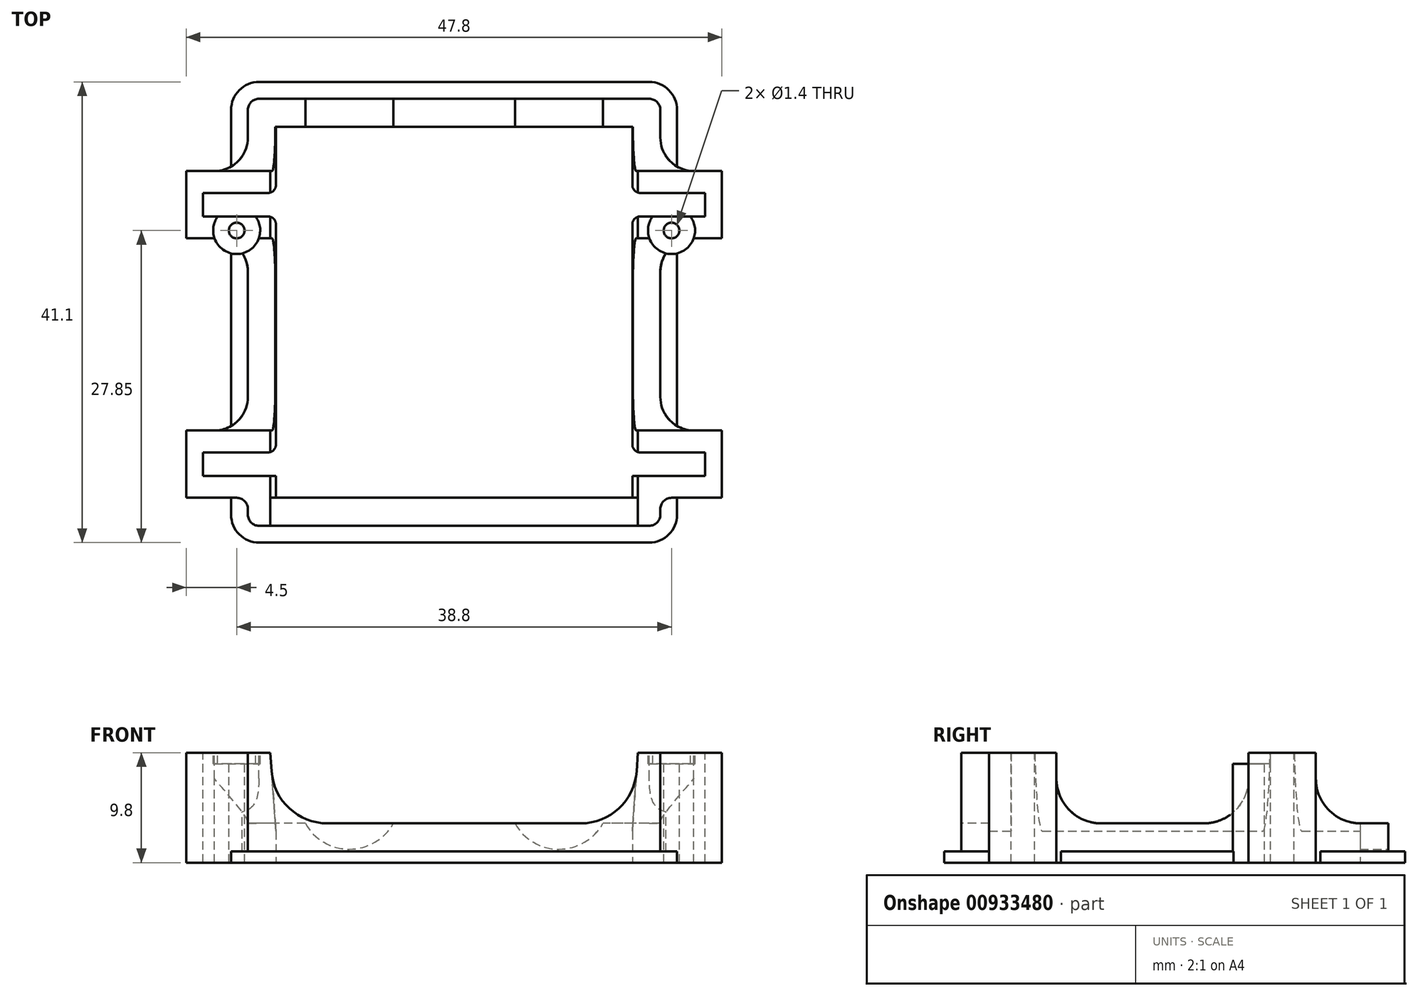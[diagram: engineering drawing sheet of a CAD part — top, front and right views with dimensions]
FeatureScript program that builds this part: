
annotation { "Feature Type Name" : "Feature", "Feature Type Description" : "" }
export const myFeature = defineFeature(function(context is Context, id is Id, definition is map)
    precondition{}
    {
        {
            assignVariable(context, id + "F0", {"name" : "ServoT", "anyValue" : 9.8});
        }
        {
            assignVariable(context, id + "F1", {"name" : "GlueEdgeH", "anyValue" : 1});
        }
        {
            var Q0;
            Q0=qCreatedBy(makeId("Top.planeOp"),FACE);
            var sketch = newSketch(context, id + "F2", { "sketchPlane" : qUnion([Q0])});
            skLineSegment(sketch, "E0.bottom", {"start": v(15.9, -16.55) * mm, "end": v(-15.9, -16.55) * mm});
            skLineSegment(sketch, "E0.top", {"start": v(15.9, 16.55) * mm, "end": v(-15.9, 16.55) * mm});
            skLineSegment(sketch, "E0.left", {"start": v(15.9, -16.55) * mm, "end": v(15.9, 16.55) * mm});
            skLineSegment(sketch, "E0.right", {"start": v(-15.9, -16.55) * mm, "end": v(-15.9, 16.55) * mm});
            skPoint(sketch, "E0.middle", {"position": v(0, 0) * mm});
            skLineSegment(sketch, "E1.0", {"start": v(17.4, 19.05) * mm, "end": v(-17.4, 19.05) * mm});
            skLineSegment(sketch, "E1.1", {"start": v(18.4, -18.05) * mm, "end": v(18.4, -17.55) * mm});
            skLineSegment(sketch, "E1.2", {"start": v(17.4, -19.05) * mm, "end": v(-17.4, -19.05) * mm});
            skLineSegment(sketch, "E1.3", {"start": v(-18.4, -18.05) * mm, "end": v(-18.4, -17.55) * mm});
            skLineSegment(sketch, "E2", {"start": v(-26.72, 9.6) * mm, "end": v(24.49, 9.6) * mm, "construction": true});
            skLineSegment(sketch, "E3", {"start": v(-23.9, 6.6) * mm, "end": v(-23.9, 12.6) * mm});
            skLineSegment(sketch, "E4", {"start": v(23.9, 6.6) * mm, "end": v(23.9, 12.6) * mm});
            skPoint(sketch, "E5", {"position": v(-23.9, 9.6) * mm});
            skPoint(sketch, "E6", {"position": v(23.9, 9.6) * mm});
            skLineSegment(sketch, "E7", {"start": v(-23.9, 12.6) * mm, "end": v(-21.4, 12.6) * mm});
            skLineSegment(sketch, "E8", {"start": v(-23.9, 6.6) * mm, "end": v(-21.4, 6.6) * mm});
            skLineSegment(sketch, "E9", {"start": v(23.9, 12.6) * mm, "end": v(21.4, 12.6) * mm});
            skLineSegment(sketch, "E10", {"start": v(23.9, 6.6) * mm, "end": v(21.4, 6.6) * mm});
            skLineSegment(sketch, "E11.trimOffspring", {"start": v(-18.4, 15.6) * mm, "end": v(-18.4, 18.05) * mm});
            skLineSegment(sketch, "E12.trimOffspring", {"start": v(18.4, 15.6) * mm, "end": v(18.4, 18.05) * mm});
            skPoint(sketch, "E13.visualSharp", {"position": v(-18.4, 6.6) * mm});
            skArc(sketch, "E13.filletArc", {"start": v(-18.4, 3.6) * mm, "mid": v(-19.28, 5.72) * mm, "end": v(-21.4, 6.6) * mm});
            skPoint(sketch, "E14.visualSharp", {"position": v(-18.4, 12.6) * mm});
            skArc(sketch, "E14.filletArc", {"start": v(-21.4, 12.6) * mm, "mid": v(-19.28, 13.48) * mm, "end": v(-18.4, 15.6) * mm});
            skPoint(sketch, "E15.visualSharp", {"position": v(18.4, 12.6) * mm});
            skArc(sketch, "E15.filletArc", {"start": v(18.4, 15.6) * mm, "mid": v(19.28, 13.48) * mm, "end": v(21.4, 12.6) * mm});
            skPoint(sketch, "E16.visualSharp", {"position": v(18.4, 6.6) * mm});
            skArc(sketch, "E16.filletArc", {"start": v(21.4, 6.6) * mm, "mid": v(19.28, 5.72) * mm, "end": v(18.4, 3.6) * mm});
            skPoint(sketch, "E17.visualSharp", {"position": v(-18.4, 19.05) * mm});
            skArc(sketch, "E17.filletArc", {"start": v(-17.4, 19.05) * mm, "mid": v(-18.1, 18.76) * mm, "end": v(-18.4, 18.05) * mm});
            skPoint(sketch, "E18.visualSharp", {"position": v(18.4, 19.05) * mm});
            skArc(sketch, "E18.filletArc", {"start": v(18.4, 18.05) * mm, "mid": v(18.1, 18.76) * mm, "end": v(17.4, 19.05) * mm});
            skPoint(sketch, "E19.visualSharp", {"position": v(18.4, -19.05) * mm});
            skArc(sketch, "E19.filletArc", {"start": v(17.4, -19.05) * mm, "mid": v(18.1, -18.76) * mm, "end": v(18.4, -18.05) * mm});
            skPoint(sketch, "E20.visualSharp", {"position": v(-18.4, -19.05) * mm});
            skArc(sketch, "E20.filletArc", {"start": v(-18.4, -18.05) * mm, "mid": v(-18.1, -18.76) * mm, "end": v(-17.4, -19.05) * mm});
            skLineSegment(sketch, "E21", {"start": v(0, -21.27) * mm, "end": v(0, 18.53) * mm, "construction": true});
            skPoint(sketch, "E21.endSnap0", {"position": v(0, -19.05) * mm});
            skLineSegment(sketch, "E22", {"start": v(-21.4, 0.48) * mm, "end": v(-21.4, 19.4) * mm, "construction": true});
            skLineSegment(sketch, "E23", {"start": v(21.4, 14.16) * mm, "end": v(21.4, -1.16) * mm, "construction": true});
            skLineSegment(sketch, "E24", {"start": v(-26.28, -13.55) * mm, "end": v(27.26, -13.55) * mm, "construction": true});
            skLineSegment(sketch, "E25", {"start": v(-23.9, -10.55) * mm, "end": v(-23.9, -16.55) * mm});
            skLineSegment(sketch, "E26", {"start": v(23.9, -10.55) * mm, "end": v(23.9, -16.55) * mm});
            skPoint(sketch, "E27", {"position": v(-23.9, -13.55) * mm});
            skPoint(sketch, "E28", {"position": v(23.9, -13.55) * mm});
            skLineSegment(sketch, "E29", {"start": v(-23.9, -10.55) * mm, "end": v(-21.4, -10.55) * mm});
            skLineSegment(sketch, "E30", {"start": v(-23.9, -16.55) * mm, "end": v(-19.4, -16.55) * mm});
            skLineSegment(sketch, "E31", {"start": v(23.9, -10.55) * mm, "end": v(21.4, -10.55) * mm});
            skLineSegment(sketch, "E32", {"start": v(23.9, -16.55) * mm, "end": v(19.4, -16.55) * mm});
            skLineSegment(sketch, "E33.trimOffspring", {"start": v(-18.4, -7.55) * mm, "end": v(-18.4, 3.6) * mm});
            skLineSegment(sketch, "E34.trimOffspring", {"start": v(18.4, -7.55) * mm, "end": v(18.4, 3.6) * mm});
            skPoint(sketch, "E35.visualSharp", {"position": v(-18.4, -10.55) * mm});
            skArc(sketch, "E35.filletArc", {"start": v(-21.4, -10.55) * mm, "mid": v(-19.28, -9.67) * mm, "end": v(-18.4, -7.55) * mm});
            skPoint(sketch, "E36.visualSharp", {"position": v(18.4, -10.55) * mm});
            skArc(sketch, "E36.filletArc", {"start": v(18.4, -7.55) * mm, "mid": v(19.28, -9.67) * mm, "end": v(21.4, -10.55) * mm});
            skPoint(sketch, "E37.visualSharp", {"position": v(-18.4, -16.55) * mm});
            skArc(sketch, "E37.filletArc", {"start": v(-18.4, -17.55) * mm, "mid": v(-18.7, -16.84) * mm, "end": v(-19.4, -16.55) * mm});
            skPoint(sketch, "E38.visualSharp", {"position": v(18.4, -16.55) * mm});
            skArc(sketch, "E38.filletArc", {"start": v(19.4, -16.55) * mm, "mid": v(18.7, -16.84) * mm, "end": v(18.4, -17.55) * mm});
            skSolve(sketch);
        }
        {
            var Q0;
            Q0=qSketchRegion(id+"F2",true);
            extrude(context, id + "F3", {"entities" : qUnion([Q0]), "depth" : (getVariable(context, 'ServoT')) * mm, "offsetDistance" : 25 * mm});
        }
        {
            var Q0;
            Q0=makeQuery(id+"F3.opExtrude","SWEPT_FACE",FACE,{"disambiguationData":[OSD([sQuery(id+"F2.wireOp",EDGE,"E1.3")])]});
            var sketch = newSketch(context, id + "F4", { "sketchPlane" : qUnion([Q0])});
            skLineSegment(sketch, "E39.0", {"start": v(-19.05, 9.8) * mm, "end": v(-19.05, 3.5) * mm});
            skLineSegment(sketch, "E40.0", {"start": v(-19.05, 9.8) * mm, "end": v(-18.05, 9.8) * mm});
            skLineSegment(sketch, "E41.0", {"start": v(-15.6, 9.8) * mm, "end": v(-18.05, 9.8) * mm});
            skLineSegment(sketch, "E42.0", {"start": v(-12.6, 9.8) * mm, "end": v(-15.6, 9.8) * mm});
            skLineSegment(sketch, "E43.0", {"start": v(-12.6, 9.8) * mm, "end": v(-12.6, 7.5) * mm});
            skLineSegment(sketch, "E44", {"start": v(-19.05, 3.5) * mm, "end": v(-16.6, 3.5) * mm});
            skPoint(sketch, "E45.visualSharp", {"position": v(-12.6, 3.5) * mm});
            skArc(sketch, "E45.filletArc", {"start": v(-16.6, 3.5) * mm, "mid": v(-13.77, 4.67) * mm, "end": v(-12.6, 7.5) * mm});
            skLineSegment(sketch, "E46", {"start": v(-2.6, 3.5) * mm, "end": v(6.55, 3.5) * mm});
            skLineSegment(sketch, "E47.0", {"start": v(-6.6, 9.8) * mm, "end": v(-6.6, 7.5) * mm});
            skLineSegment(sketch, "E48.0", {"start": v(10.55, 9.8) * mm, "end": v(10.55, 7.5) * mm});
            skLineSegment(sketch, "E49.0", {"start": v(7.55, 9.8) * mm, "end": v(-6.6, 9.8) * mm});
            skLineSegment(sketch, "E50.0", {"start": v(10.55, 9.8) * mm, "end": v(7.55, 9.8) * mm});
            skPoint(sketch, "E51.orphan", {"position": v(10.55, 0) * mm});
            skPoint(sketch, "E52.visualSharp", {"position": v(10.55, 3.5) * mm});
            skArc(sketch, "E52.filletArc", {"start": v(6.55, 3.5) * mm, "mid": v(9.38, 4.67) * mm, "end": v(10.55, 7.5) * mm});
            skPoint(sketch, "E53.visualSharp", {"position": v(-6.6, 3.5) * mm});
            skArc(sketch, "E53.filletArc", {"start": v(-6.6, 7.5) * mm, "mid": v(-5.43, 4.67) * mm, "end": v(-2.6, 3.5) * mm});
            skSolve(sketch);
        }
        {
            var Q0;
            Q0=qSketchRegion(id+"F4",true);
            extrude(context, id + "F5", {"entities" : qUnion([Q0]), "operationType" : NewBodyOperationType.REMOVE, "endBound" : BoundingType.THROUGH_ALL, "oppositeDirection" : true, "depth" : 25 * mm, "offsetDistance" : 25 * mm, "hasSecondDirection" : true, "secondDirectionBound" : SecondDirectionBoundingType.THROUGH_ALL, "secondDirectionOppositeDirection" : false, "secondDirectionDepth" : 25 * mm});
        }
        {
            var Q0;
            Q0=makeQuery(id+"F3.opExtrude","CAP_FACE",FACE,{"disambiguationData":[OSD([sQuery(id+"F2.wireOp",EDGE,"E0.bottom"),sQuery(id+"F2.wireOp",EDGE,"E0.top"),sQuery(id+"F2.wireOp",EDGE,"E0.left"),sQuery(id+"F2.wireOp",EDGE,"E0.right"),sQuery(id+"F2.wireOp",EDGE,"E1.0"),sQuery(id+"F2.wireOp",EDGE,"E1.1"),sQuery(id+"F2.wireOp",EDGE,"E1.2"),sQuery(id+"F2.wireOp",EDGE,"E1.3"),sQuery(id+"F2.wireOp",EDGE,"E3"),sQuery(id+"F2.wireOp",EDGE,"E4"),sQuery(id+"F2.wireOp",EDGE,"E7"),sQuery(id+"F2.wireOp",EDGE,"E8"),sQuery(id+"F2.wireOp",EDGE,"E9"),sQuery(id+"F2.wireOp",EDGE,"E10"),sQuery(id+"F2.wireOp",EDGE,"E11.trimOffspring"),sQuery(id+"F2.wireOp",EDGE,"E12.trimOffspring"),sQuery(id+"F2.wireOp",EDGE,"E13.filletArc"),sQuery(id+"F2.wireOp",EDGE,"E14.filletArc"),sQuery(id+"F2.wireOp",EDGE,"E15.filletArc"),sQuery(id+"F2.wireOp",EDGE,"E16.filletArc"),sQuery(id+"F2.wireOp",EDGE,"E17.filletArc"),sQuery(id+"F2.wireOp",EDGE,"E18.filletArc"),sQuery(id+"F2.wireOp",EDGE,"E19.filletArc"),sQuery(id+"F2.wireOp",EDGE,"E20.filletArc")])],"isStart":true});
            var sketch = newSketch(context, id + "F6", { "sketchPlane" : qUnion([Q0])});
            skLineSegment(sketch, "E54.0", {"start": v(17.4, 19.05) * mm, "end": v(-17.4, 19.05) * mm});
            skArc(sketch, "E55.0", {"start": v(-18.4, 18.05) * mm, "mid": v(-18.1, 18.76) * mm, "end": v(-17.4, 19.05) * mm});
            skLineSegment(sketch, "E56.0", {"start": v(-18.4, 18.05) * mm, "end": v(-18.4, -6.6) * mm});
            skArc(sketch, "E57.0", {"start": v(17.4, 19.05) * mm, "mid": v(18.1, 18.76) * mm, "end": v(18.4, 18.05) * mm});
            skLineSegment(sketch, "E58.0", {"start": v(18.4, 18.05) * mm, "end": v(18.4, -6.6) * mm});
            skLineSegment(sketch, "E59.0", {"start": v(18.4, -12.6) * mm, "end": v(18.4, -18.05) * mm});
            skArc(sketch, "E60.0", {"start": v(18.4, -18.05) * mm, "mid": v(18.1, -18.76) * mm, "end": v(17.4, -19.05) * mm});
            skLineSegment(sketch, "E61.0", {"start": v(17.4, -19.05) * mm, "end": v(-17.4, -19.05) * mm});
            skArc(sketch, "E62.0", {"start": v(-17.4, -19.05) * mm, "mid": v(-18.1, -18.76) * mm, "end": v(-18.4, -18.05) * mm});
            skLineSegment(sketch, "E63.0", {"start": v(-18.4, -12.6) * mm, "end": v(-18.4, -18.05) * mm});
            skLineSegment(sketch, "E64.0", {"start": v(-19.9, 18.05) * mm, "end": v(-19.9, -6.6) * mm});
            skLineSegment(sketch, "E64.1", {"start": v(19.9, 18.05) * mm, "end": v(19.9, -6.6) * mm});
            skArc(sketch, "E64.2", {"start": v(17.4, 20.55) * mm, "mid": v(19.17, 19.82) * mm, "end": v(19.9, 18.05) * mm});
            skLineSegment(sketch, "E64.3", {"start": v(17.4, 20.55) * mm, "end": v(-17.4, 20.55) * mm});
            skArc(sketch, "E64.4", {"start": v(-19.9, 18.05) * mm, "mid": v(-19.17, 19.82) * mm, "end": v(-17.4, 20.55) * mm});
            skLineSegment(sketch, "E65.0", {"start": v(19.9, -12.6) * mm, "end": v(19.9, -18.05) * mm});
            skLineSegment(sketch, "E65.1", {"start": v(-19.9, -12.6) * mm, "end": v(-19.9, -18.05) * mm});
            skArc(sketch, "E65.2", {"start": v(-17.4, -20.55) * mm, "mid": v(-19.17, -19.82) * mm, "end": v(-19.9, -18.05) * mm});
            skLineSegment(sketch, "E65.3", {"start": v(17.4, -20.55) * mm, "end": v(-17.4, -20.55) * mm});
            skArc(sketch, "E65.4", {"start": v(19.9, -18.05) * mm, "mid": v(19.17, -19.82) * mm, "end": v(17.4, -20.55) * mm});
            skLineSegment(sketch, "E66", {"start": v(-18.4, -6.6) * mm, "end": v(-19.9, -6.6) * mm});
            skLineSegment(sketch, "E67", {"start": v(-18.4, -12.6) * mm, "end": v(-19.9, -12.6) * mm});
            skLineSegment(sketch, "E68", {"start": v(19.9, -12.6) * mm, "end": v(18.4, -12.6) * mm});
            skLineSegment(sketch, "E69", {"start": v(19.9, -6.6) * mm, "end": v(18.4, -6.6) * mm});
            skSolve(sketch);
        }
        {
            var Q0;
            Q0=qSketchRegion(id+"F6",true);
            extrude(context, id + "F7", {"entities" : qUnion([Q0]), "operationType" : NewBodyOperationType.ADD, "oppositeDirection" : true, "depth" : (getVariable(context, 'GlueEdgeH')) * mm, "offsetDistance" : 25 * mm});
        }
        {
            var Q0;
            {var subQ0=sQuery(id+"F2.wireOp",EDGE,"E0.right");var subQ1=sQuery(id+"F2.wireOp",EDGE,"E13.filletArc");var subQ2=sQuery(id+"F2.wireOp",EDGE,"E3");Q0=makeQuery(id+"F5.boolean.opBoolean","SPLIT",FACE,{"disambiguationData":[TD([makeQuery(id+"F3.opExtrude","SWEPT_FACE",FACE,{"disambiguationData":[OSD([subQ0])]})])],"derivedFrom":makeQuery(id+"F3.opExtrude","CAP_FACE",FACE,{"disambiguationData":[OSD([sQuery(id+"F2.wireOp",EDGE,"E0.bottom"),sQuery(id+"F2.wireOp",EDGE,"E0.top"),sQuery(id+"F2.wireOp",EDGE,"E0.left"),subQ0,sQuery(id+"F2.wireOp",EDGE,"E1.0"),sQuery(id+"F2.wireOp",EDGE,"E1.1"),sQuery(id+"F2.wireOp",EDGE,"E1.2"),sQuery(id+"F2.wireOp",EDGE,"E1.3"),subQ2,sQuery(id+"F2.wireOp",EDGE,"E4"),sQuery(id+"F2.wireOp",EDGE,"E11.trimOffspring"),sQuery(id+"F2.wireOp",EDGE,"E12.trimOffspring"),subQ1,sQuery(id+"F2.wireOp",EDGE,"E14.filletArc"),sQuery(id+"F2.wireOp",EDGE,"E15.filletArc"),sQuery(id+"F2.wireOp",EDGE,"E16.filletArc"),sQuery(id+"F2.wireOp",EDGE,"E17.filletArc"),sQuery(id+"F2.wireOp",EDGE,"E18.filletArc"),sQuery(id+"F2.wireOp",EDGE,"E19.filletArc"),sQuery(id+"F2.wireOp",EDGE,"E20.filletArc")])],"isStart":false})});}
            var sketch = newSketch(context, id + "F8", { "sketchPlane" : qUnion([Q0])});
            skLineSegment(sketch, "E70.0", {"start": v(-26.72, 9.6) * mm, "end": v(24.49, 9.6) * mm, "construction": true});
            skLineSegment(sketch, "E71.0", {"start": v(-15.9, 8.55) * mm, "end": v(-15.9, 10.65) * mm});
            skLineSegment(sketch, "E72.0", {"start": v(15.9, 8.55) * mm, "end": v(15.9, 10.65) * mm});
            skLineSegment(sketch, "E73", {"start": v(-22.4, 10.65) * mm, "end": v(-15.9, 10.65) * mm});
            skLineSegment(sketch, "E74", {"start": v(-22.4, 8.55) * mm, "end": v(-15.9, 8.55) * mm});
            skLineSegment(sketch, "E75", {"start": v(15.9, 10.65) * mm, "end": v(22.4, 10.65) * mm});
            skLineSegment(sketch, "E76", {"start": v(15.9, 8.55) * mm, "end": v(22.4, 8.55) * mm});
            skPoint(sketch, "E77.orphan", {"position": v(-23.9, 12.6) * mm});
            skPoint(sketch, "E78.orphan", {"position": v(-23.9, 6.6) * mm});
            skPoint(sketch, "E79.orphan", {"position": v(23.9, 12.6) * mm});
            skPoint(sketch, "E80.orphan", {"position": v(23.9, 6.6) * mm});
            skLineSegment(sketch, "E81", {"start": v(-22.4, 10.65) * mm, "end": v(-22.4, 8.55) * mm});
            skPoint(sketch, "E82", {"position": v(-15.9, 9.6) * mm});
            skPoint(sketch, "E83", {"position": v(15.9, 9.6) * mm});
            skLineSegment(sketch, "E84", {"start": v(22.4, 10.65) * mm, "end": v(22.4, 8.55) * mm});
            skLineSegment(sketch, "E85.0", {"start": v(-26.28, -13.55) * mm, "end": v(27.26, -13.55) * mm, "construction": true});
            skLineSegment(sketch, "E86", {"start": v(-22.4, -12.5) * mm, "end": v(-22.4, -14.6) * mm});
            skLineSegment(sketch, "E87", {"start": v(22.4, -12.5) * mm, "end": v(22.4, -14.6) * mm});
            skPoint(sketch, "E88", {"position": v(-22.4, -13.55) * mm});
            skPoint(sketch, "E89", {"position": v(22.4, -13.55) * mm});
            skLineSegment(sketch, "E90", {"start": v(-22.4, -12.5) * mm, "end": v(-15.9, -12.5) * mm});
            skLineSegment(sketch, "E91", {"start": v(22.4, -14.6) * mm, "end": v(15.9, -14.6) * mm});
            skLineSegment(sketch, "E92.0", {"start": v(-15.9, -14.6) * mm, "end": v(-15.9, -12.5) * mm});
            skLineSegment(sketch, "E93.0", {"start": v(15.9, -14.6) * mm, "end": v(15.9, -12.5) * mm});
            skLineSegment(sketch, "E94.trimOffspring", {"start": v(15.9, -12.5) * mm, "end": v(22.4, -12.5) * mm});
            skLineSegment(sketch, "E95.trimOffspring", {"start": v(-15.9, -14.6) * mm, "end": v(-22.4, -14.6) * mm});
            skSolve(sketch);
        }
        {
            var Q0;
            Q0=qSketchRegion(id+"F8",true);
            extrude(context, id + "F9", {"entities" : qUnion([Q0]), "operationType" : NewBodyOperationType.REMOVE, "oppositeDirection" : true, "depth" : (getVariable(context, 'ServoT')) * mm, "offsetDistance" : 25 * mm});
        }
        {
            var Q0;
            {var subQ1=sQuery(id+"F2.wireOp",EDGE,"E7");var subQ2=sQuery(id+"F2.wireOp",EDGE,"E0.right");var subQ4=makeQuery(id+"F3.opExtrude","SWEPT_FACE",FACE,{"disambiguationData":[OSD([subQ1])]});Q0=makeQuery(id+"F9.boolean.opBoolean","SPLIT",EDGE,{"disambiguationData":[TD([subQ4])],"derivedFrom":makeQuery(id+"F5.boolean.opBoolean","SPLIT",EDGE,{"disambiguationData":[TD([subQ4])],"derivedFrom":makeQuery(id+"F3.opExtrude","CAP_EDGE",EDGE,{"disambiguationData":[OSD([subQ2])],"isStart":false})})});}
            var Q1;
            {var subQ0=sQuery(id+"F2.wireOp",EDGE,"E8");var subQ1=sQuery(id+"F2.wireOp",EDGE,"E7");var subQ2=sQuery(id+"F2.wireOp",EDGE,"E0.right");var subQ5=makeQuery(id+"F3.opExtrude","SWEPT_FACE",FACE,{"disambiguationData":[OSD([subQ0])]});Q1=makeQuery(id+"F9.boolean.opBoolean","SPLIT",EDGE,{"disambiguationData":[TD([subQ5])],"derivedFrom":makeQuery(id+"F5.boolean.opBoolean","SPLIT",EDGE,{"disambiguationData":[TD([makeQuery(id+"F3.opExtrude","SWEPT_FACE",FACE,{"disambiguationData":[OSD([subQ1])]})])],"derivedFrom":makeQuery(id+"F3.opExtrude","CAP_EDGE",EDGE,{"disambiguationData":[OSD([subQ2])],"isStart":false})})});}
            var Q2;
            {var subQ0=sQuery(id+"F2.wireOp",EDGE,"E29");var subQ1=sQuery(id+"F2.wireOp",EDGE,"E0.right");var subQ2=sQuery(id+"F2.wireOp",EDGE,"E0.bottom");var subQ5=makeQuery(id+"F3.opExtrude","SWEPT_FACE",FACE,{"disambiguationData":[OSD([subQ0])]});Q2=makeQuery(id+"F9.boolean.opBoolean","SPLIT",EDGE,{"disambiguationData":[TD([subQ5])],"derivedFrom":makeQuery(id+"F5.boolean.opBoolean","SPLIT",EDGE,{"disambiguationData":[TD([makeQuery(id+"F3.opExtrude","SWEPT_FACE",FACE,{"disambiguationData":[OSD([subQ2])]})])],"derivedFrom":makeQuery(id+"F3.opExtrude","CAP_EDGE",EDGE,{"disambiguationData":[OSD([subQ1])],"isStart":false})})});}
            var Q3;
            {var subQ0=sQuery(id+"F2.wireOp",EDGE,"E0.bottom");var subQ1=makeQuery(id+"F3.opExtrude","SWEPT_FACE",FACE,{"disambiguationData":[OSD([subQ0])]});var subQ2=sQuery(id+"F2.wireOp",EDGE,"E0.right");Q3=makeQuery(id+"F9.boolean.opBoolean","SPLIT",EDGE,{"disambiguationData":[TD([subQ1])],"derivedFrom":makeQuery(id+"F5.boolean.opBoolean","SPLIT",EDGE,{"disambiguationData":[TD([subQ1])],"derivedFrom":makeQuery(id+"F3.opExtrude","CAP_EDGE",EDGE,{"disambiguationData":[OSD([subQ2])],"isStart":false})})});}
            chamfer(context, id + "F10", {"entities" : qUnion([Q0, Q1, Q2, Q3]), "chamferType" : ChamferType.TWO_OFFSETS, "width1" : 0.5 * mm, "oppositeDirection" : false, "width2" : 7 * mm, "tangentPropagation" : true});
        }
        {
            var Q0;
            {var subQ0=sQuery(id+"F2.wireOp",EDGE,"E10");var subQ1=sQuery(id+"F2.wireOp",EDGE,"E9");var subQ2=sQuery(id+"F2.wireOp",EDGE,"E0.left");var subQ5=makeQuery(id+"F3.opExtrude","SWEPT_FACE",FACE,{"disambiguationData":[OSD([subQ0])]});Q0=makeQuery(id+"F9.boolean.opBoolean","SPLIT",EDGE,{"disambiguationData":[TD([subQ5])],"derivedFrom":makeQuery(id+"F5.boolean.opBoolean","SPLIT",EDGE,{"disambiguationData":[TD([makeQuery(id+"F3.opExtrude","SWEPT_FACE",FACE,{"disambiguationData":[OSD([subQ1])]})])],"derivedFrom":makeQuery(id+"F3.opExtrude","CAP_EDGE",EDGE,{"disambiguationData":[OSD([subQ2])],"isStart":false})})});}
            var Q1;
            {var subQ1=sQuery(id+"F2.wireOp",EDGE,"E9");var subQ2=sQuery(id+"F2.wireOp",EDGE,"E0.left");var subQ5=makeQuery(id+"F3.opExtrude","SWEPT_FACE",FACE,{"disambiguationData":[OSD([subQ1])]});Q1=makeQuery(id+"F9.boolean.opBoolean","SPLIT",EDGE,{"disambiguationData":[TD([subQ5])],"derivedFrom":makeQuery(id+"F5.boolean.opBoolean","SPLIT",EDGE,{"disambiguationData":[TD([subQ5])],"derivedFrom":makeQuery(id+"F3.opExtrude","CAP_EDGE",EDGE,{"disambiguationData":[OSD([subQ2])],"isStart":false})})});}
            var Q2;
            {var subQ0=sQuery(id+"F2.wireOp",EDGE,"E0.bottom");var subQ1=makeQuery(id+"F3.opExtrude","SWEPT_FACE",FACE,{"disambiguationData":[OSD([subQ0])]});var subQ3=sQuery(id+"F2.wireOp",EDGE,"E0.left");Q2=makeQuery(id+"F9.boolean.opBoolean","SPLIT",EDGE,{"disambiguationData":[TD([subQ1])],"derivedFrom":makeQuery(id+"F5.boolean.opBoolean","SPLIT",EDGE,{"disambiguationData":[TD([subQ1])],"derivedFrom":makeQuery(id+"F3.opExtrude","CAP_EDGE",EDGE,{"disambiguationData":[OSD([subQ3])],"isStart":false})})});}
            chamfer(context, id + "F11", {"entities" : qUnion([Q0, Q1, Q2]), "chamferType" : ChamferType.TWO_OFFSETS, "width1" : 7 * mm, "oppositeDirection" : false, "width2" : 0.5 * mm, "tangentPropagation" : true});
        }
        {
            var Q0;
            Q0=makeQuery(id+"F9.boolean.opBoolean","COPY",EDGE,{"derivedFrom":makeQuery(id+"F9.opExtrude","SWEPT_EDGE",EDGE,{"disambiguationData":[OSD([sQuery(id+"F2.wireOp",EDGE,"E0.right"),sQuery(id+"F8.wireOp",EDGE,"E71.0"),sQuery(id+"F8.wireOp",EDGE,"E73")])]})});
            var Q1;
            Q1=makeQuery(id+"F9.boolean.opBoolean","COPY",EDGE,{"derivedFrom":makeQuery(id+"F9.opExtrude","SWEPT_EDGE",EDGE,{"disambiguationData":[OSD([sQuery(id+"F8.wireOp",EDGE,"E72.0"),sQuery(id+"F8.wireOp",EDGE,"E75")])]})});
            var Q2;
            Q2=makeQuery(id+"F9.boolean.opBoolean","COPY",EDGE,{"derivedFrom":makeQuery(id+"F9.opExtrude","SWEPT_EDGE",EDGE,{"disambiguationData":[OSD([sQuery(id+"F2.wireOp",EDGE,"E0.right"),sQuery(id+"F8.wireOp",EDGE,"E71.0"),sQuery(id+"F8.wireOp",EDGE,"E74")])]})});
            var Q3;
            Q3=makeQuery(id+"F9.boolean.opBoolean","COPY",EDGE,{"derivedFrom":makeQuery(id+"F9.opExtrude","SWEPT_EDGE",EDGE,{"disambiguationData":[OSD([sQuery(id+"F8.wireOp",EDGE,"E72.0"),sQuery(id+"F8.wireOp",EDGE,"E76")])]})});
            var Q4;
            Q4=makeQuery(id+"F9.boolean.opBoolean","COPY",EDGE,{"derivedFrom":makeQuery(id+"F9.opExtrude","SWEPT_EDGE",EDGE,{"disambiguationData":[OSD([sQuery(id+"F8.wireOp",EDGE,"E90"),sQuery(id+"F8.wireOp",EDGE,"E92.0")])]})});
            var Q5;
            Q5=makeQuery(id+"F9.boolean.opBoolean","COPY",EDGE,{"derivedFrom":makeQuery(id+"F9.opExtrude","SWEPT_EDGE",EDGE,{"disambiguationData":[OSD([sQuery(id+"F8.wireOp",EDGE,"E92.0"),sQuery(id+"F8.wireOp",EDGE,"E95.trimOffspring")])]})});
            var Q6;
            Q6=makeQuery(id+"F9.boolean.opBoolean","COPY",EDGE,{"derivedFrom":makeQuery(id+"F9.opExtrude","SWEPT_EDGE",EDGE,{"disambiguationData":[OSD([sQuery(id+"F8.wireOp",EDGE,"E91"),sQuery(id+"F8.wireOp",EDGE,"E93.0")])]})});
            var Q7;
            Q7=makeQuery(id+"F9.boolean.opBoolean","COPY",EDGE,{"derivedFrom":makeQuery(id+"F9.opExtrude","SWEPT_EDGE",EDGE,{"disambiguationData":[OSD([sQuery(id+"F8.wireOp",EDGE,"E93.0"),sQuery(id+"F8.wireOp",EDGE,"E94.trimOffspring")])]})});
            fillet(context, id + "F12", {"entities" : qUnion([Q0, Q1, Q2, Q3, Q4, Q5, Q6, Q7]), "radius" : 0.7 * mm, "tangentPropagation" : true, "allowEdgeOverflow" : false});
        }
        {
            var Q0;
            Q0=makeQuery(id+"F3.opExtrude","SWEPT_FACE",FACE,{"disambiguationData":[OSD([sQuery(id+"F2.wireOp",EDGE,"E1.0")])]});
            var sketch = newSketch(context, id + "F13", { "sketchPlane" : qUnion([Q0])});
            skLineSegment(sketch, "E96", {"start": v(0, -7.25) * mm, "end": v(0, 20.62) * mm, "construction": true});
            skLineSegment(sketch, "E97", {"start": v(-9.35, 11.18) * mm, "end": v(-9.35, -5.6) * mm, "construction": true});
            skLineSegment(sketch, "E98", {"start": v(9.35, 10.84) * mm, "end": v(9.35, -4.34) * mm, "construction": true});
            skLineSegment(sketch, "E99", {"start": v(-13.01, 1.2) * mm, "end": v(13.24, 1.2) * mm, "construction": true});
            skArc(sketch, "E100", {"start": v(-13.28, 3.5) * mm, "mid": v(-9.35, 1.2) * mm, "end": v(-5.42, 3.5) * mm});
            skArc(sketch, "E101", {"start": v(5.42, 3.5) * mm, "mid": v(9.35, 1.2) * mm, "end": v(13.28, 3.5) * mm});
            skLineSegment(sketch, "E102.0", {"start": v(-13.28, 3.5) * mm, "end": v(-5.42, 3.5) * mm});
            skPoint(sketch, "E103.orphan", {"position": v(17.4, 3.5) * mm});
            skLineSegment(sketch, "E104.trimOffspring", {"start": v(5.42, 3.5) * mm, "end": v(13.28, 3.5) * mm});
            skPoint(sketch, "E105.orphan", {"position": v(-17.4, 3.5) * mm});
            skPoint(sketch, "E106.0", {"position": v(0, 0) * mm});
            skSolve(sketch);
        }
        {
            var Q0;
            Q0=qSketchRegion(id+"F13",true);
            extrude(context, id + "F14", {"entities" : qUnion([Q0]), "operationType" : NewBodyOperationType.REMOVE, "endBound" : BoundingType.UP_TO_NEXT, "oppositeDirection" : true, "depth" : 25 * mm, "offsetDistance" : 25 * mm});
        }
        {
            var Q0;
            {var subQ0=sQuery(id+"F2.wireOp",EDGE,"E8");var subQ1=sQuery(id+"F2.wireOp",EDGE,"E7");var subQ2=sQuery(id+"F2.wireOp",EDGE,"E3");var subQ3=sQuery(id+"F2.wireOp",EDGE,"E0.right");var subQ4=sQuery(id+"F2.wireOp",EDGE,"E13.filletArc");Q0=makeQuery(id+"F5.boolean.opBoolean","SPLIT",FACE,{"disambiguationData":[TD([makeQuery(id+"F3.opExtrude","SWEPT_FACE",FACE,{"disambiguationData":[OSD([subQ3])]})])],"derivedFrom":makeQuery(id+"F3.opExtrude","CAP_FACE",FACE,{"disambiguationData":[OSD([sQuery(id+"F2.wireOp",EDGE,"E0.bottom"),sQuery(id+"F2.wireOp",EDGE,"E0.top"),sQuery(id+"F2.wireOp",EDGE,"E0.left"),subQ3,sQuery(id+"F2.wireOp",EDGE,"E1.0"),sQuery(id+"F2.wireOp",EDGE,"E1.1"),sQuery(id+"F2.wireOp",EDGE,"E1.2"),sQuery(id+"F2.wireOp",EDGE,"E1.3"),subQ2,sQuery(id+"F2.wireOp",EDGE,"E4"),subQ1,subQ0,sQuery(id+"F2.wireOp",EDGE,"E9"),sQuery(id+"F2.wireOp",EDGE,"E10"),sQuery(id+"F2.wireOp",EDGE,"E11.trimOffspring"),sQuery(id+"F2.wireOp",EDGE,"E12.trimOffspring"),subQ4,sQuery(id+"F2.wireOp",EDGE,"E14.filletArc"),sQuery(id+"F2.wireOp",EDGE,"E15.filletArc"),sQuery(id+"F2.wireOp",EDGE,"E16.filletArc"),sQuery(id+"F2.wireOp",EDGE,"E17.filletArc"),sQuery(id+"F2.wireOp",EDGE,"E18.filletArc"),sQuery(id+"F2.wireOp",EDGE,"E19.filletArc"),sQuery(id+"F2.wireOp",EDGE,"E20.filletArc")])],"isStart":false})});}
            var sketch = newSketch(context, id + "F15", { "sketchPlane" : qUnion([Q0])});
            skLineSegment(sketch, "E107.0", {"start": v(-26.72, 9.6) * mm, "end": v(24.49, 9.6) * mm, "construction": true});
            skLineSegment(sketch, "E108", {"start": v(-25.63, 7.3) * mm, "end": v(27.66, 7.3) * mm, "construction": true});
            skLineSegment(sketch, "E109", {"start": v(-19.4, 14.21) * mm, "end": v(-19.4, -2.2) * mm, "construction": true});
            skLineSegment(sketch, "E110", {"start": v(19.4, 13.45) * mm, "end": v(19.4, -2.85) * mm, "construction": true});
            skArc(sketch, "E111", {"start": v(-21.09, 8.55) * mm, "mid": v(-19.4, 5.2) * mm, "end": v(-17.71, 8.55) * mm});
            skArc(sketch, "E112", {"start": v(17.71, 8.55) * mm, "mid": v(19.4, 5.2) * mm, "end": v(21.09, 8.55) * mm});
            skLineSegment(sketch, "E113.0", {"start": v(-21.09, 8.55) * mm, "end": v(-17.71, 8.55) * mm});
            skPoint(sketch, "E114.orphan", {"position": v(-22.4, 8.55) * mm});
            skPoint(sketch, "E115.orphan", {"position": v(-16.6, 8.55) * mm});
            skLineSegment(sketch, "E116.0", {"start": v(17.71, 8.55) * mm, "end": v(21.09, 8.55) * mm});
            skPoint(sketch, "E117.orphan", {"position": v(16.6, 8.55) * mm});
            skPoint(sketch, "E118.orphan", {"position": v(22.4, 8.55) * mm});
            skSolve(sketch);
        }
        {
            var Q0;
            Q0=qSketchRegion(id+"F15",true);
            var Q1;
            Q1=makeQuery(id+"F7.boolean.opBoolean","MERGE",FACE,{"derivedFrom":[makeQuery(id+"F3.opExtrude","CAP_FACE",FACE,{"disambiguationData":[OSD([sQuery(id+"F2.wireOp",EDGE,"E0.bottom"),sQuery(id+"F2.wireOp",EDGE,"E0.top"),sQuery(id+"F2.wireOp",EDGE,"E0.left"),sQuery(id+"F2.wireOp",EDGE,"E0.right"),sQuery(id+"F2.wireOp",EDGE,"E1.0"),sQuery(id+"F2.wireOp",EDGE,"E1.1"),sQuery(id+"F2.wireOp",EDGE,"E1.2"),sQuery(id+"F2.wireOp",EDGE,"E1.3"),sQuery(id+"F2.wireOp",EDGE,"E3"),sQuery(id+"F2.wireOp",EDGE,"E4"),sQuery(id+"F2.wireOp",EDGE,"E7"),sQuery(id+"F2.wireOp",EDGE,"E8"),sQuery(id+"F2.wireOp",EDGE,"E9"),sQuery(id+"F2.wireOp",EDGE,"E10"),sQuery(id+"F2.wireOp",EDGE,"E11.trimOffspring"),sQuery(id+"F2.wireOp",EDGE,"E12.trimOffspring"),sQuery(id+"F2.wireOp",EDGE,"E13.filletArc"),sQuery(id+"F2.wireOp",EDGE,"E14.filletArc"),sQuery(id+"F2.wireOp",EDGE,"E15.filletArc"),sQuery(id+"F2.wireOp",EDGE,"E16.filletArc"),sQuery(id+"F2.wireOp",EDGE,"E17.filletArc"),sQuery(id+"F2.wireOp",EDGE,"E18.filletArc"),sQuery(id+"F2.wireOp",EDGE,"E19.filletArc"),sQuery(id+"F2.wireOp",EDGE,"E20.filletArc")])],"isStart":true}),makeQuery(id+"F7.opExtrude","CAP_FACE",FACE,{"disambiguationData":[OSD([sQuery(id+"F6.wireOp",EDGE,"E54.0"),sQuery(id+"F6.wireOp",EDGE,"E55.0"),sQuery(id+"F6.wireOp",EDGE,"E56.0"),sQuery(id+"F6.wireOp",EDGE,"E57.0"),sQuery(id+"F6.wireOp",EDGE,"E58.0"),sQuery(id+"F6.wireOp",EDGE,"E64.0"),sQuery(id+"F6.wireOp",EDGE,"E64.1"),sQuery(id+"F6.wireOp",EDGE,"E64.2"),sQuery(id+"F6.wireOp",EDGE,"E64.3"),sQuery(id+"F6.wireOp",EDGE,"E64.4"),sQuery(id+"F6.wireOp",EDGE,"E66"),sQuery(id+"F6.wireOp",EDGE,"E69")])],"isStart":true}),makeQuery(id+"F7.opExtrude","CAP_FACE",FACE,{"disambiguationData":[OSD([sQuery(id+"F6.wireOp",EDGE,"E59.0"),sQuery(id+"F6.wireOp",EDGE,"E60.0"),sQuery(id+"F6.wireOp",EDGE,"E61.0"),sQuery(id+"F6.wireOp",EDGE,"E62.0"),sQuery(id+"F6.wireOp",EDGE,"E63.0"),sQuery(id+"F6.wireOp",EDGE,"E65.0"),sQuery(id+"F6.wireOp",EDGE,"E65.1"),sQuery(id+"F6.wireOp",EDGE,"E65.2"),sQuery(id+"F6.wireOp",EDGE,"E65.3"),sQuery(id+"F6.wireOp",EDGE,"E65.4"),sQuery(id+"F6.wireOp",EDGE,"E67"),sQuery(id+"F6.wireOp",EDGE,"E68")])],"isStart":true})]});
            extrude(context, id + "F16", {"entities" : qUnion([Q0]), "operationType" : NewBodyOperationType.ADD, "endBound" : BoundingType.UP_TO_SURFACE, "oppositeDirection" : true, "depth" : 25 * mm, "endBoundEntityFace" : qUnion([Q1]), "offsetDistance" : 25 * mm});
        }
        {
            var Q0;
            {var subQ0=sQuery(id+"F2.wireOp",EDGE,"E8");var subQ1=sQuery(id+"F2.wireOp",EDGE,"E7");var subQ2=sQuery(id+"F2.wireOp",EDGE,"E3");var subQ3=sQuery(id+"F2.wireOp",EDGE,"E0.right");var subQ4=sQuery(id+"F2.wireOp",EDGE,"E13.filletArc");Q0=makeQuery(id+"F16.boolean.opBoolean","MERGE",FACE,{"derivedFrom":[makeQuery(id+"F5.boolean.opBoolean","SPLIT",FACE,{"disambiguationData":[TD([makeQuery(id+"F3.opExtrude","SWEPT_FACE",FACE,{"disambiguationData":[OSD([subQ3])]})])],"derivedFrom":makeQuery(id+"F3.opExtrude","CAP_FACE",FACE,{"disambiguationData":[OSD([sQuery(id+"F2.wireOp",EDGE,"E0.bottom"),sQuery(id+"F2.wireOp",EDGE,"E0.top"),sQuery(id+"F2.wireOp",EDGE,"E0.left"),subQ3,sQuery(id+"F2.wireOp",EDGE,"E1.0"),sQuery(id+"F2.wireOp",EDGE,"E1.1"),sQuery(id+"F2.wireOp",EDGE,"E1.2"),sQuery(id+"F2.wireOp",EDGE,"E1.3"),subQ2,sQuery(id+"F2.wireOp",EDGE,"E4"),subQ1,subQ0,sQuery(id+"F2.wireOp",EDGE,"E9"),sQuery(id+"F2.wireOp",EDGE,"E10"),sQuery(id+"F2.wireOp",EDGE,"E11.trimOffspring"),sQuery(id+"F2.wireOp",EDGE,"E12.trimOffspring"),subQ4,sQuery(id+"F2.wireOp",EDGE,"E14.filletArc"),sQuery(id+"F2.wireOp",EDGE,"E15.filletArc"),sQuery(id+"F2.wireOp",EDGE,"E16.filletArc"),sQuery(id+"F2.wireOp",EDGE,"E17.filletArc"),sQuery(id+"F2.wireOp",EDGE,"E18.filletArc"),sQuery(id+"F2.wireOp",EDGE,"E19.filletArc"),sQuery(id+"F2.wireOp",EDGE,"E20.filletArc")])],"isStart":false})}),makeQuery(id+"F16.opExtrude","CAP_FACE",FACE,{"disambiguationData":[OSD([sQuery(id+"F15.wireOp",EDGE,"E111"),sQuery(id+"F15.wireOp",EDGE,"E113.0")])],"isStart":true})]});}
            var sketch = newSketch(context, id + "F17", { "sketchPlane" : qUnion([Q0])});
            skLineSegment(sketch, "E119.0", {"start": v(-25.63, 7.3) * mm, "end": v(27.66, 7.3) * mm, "construction": true});
            skLineSegment(sketch, "E120.0", {"start": v(-19.4, 14.21) * mm, "end": v(-19.4, -2.2) * mm, "construction": true});
            skCircle(sketch, "E121", {"center": v(-19.4, 7.3) * mm, "radius": 0.7 * mm});
            skPoint(sketch, "E122.0", {"position": v(19.4, 7.3) * mm});
            skCircle(sketch, "E123", {"center": v(19.4, 7.3) * mm, "radius": 0.7 * mm});
            skSolve(sketch);
        }
        {
            var Q0;
            Q0=qSketchRegion(id+"F17",true);
            extrude(context, id + "F18", {"entities" : qUnion([Q0]), "operationType" : NewBodyOperationType.REMOVE, "endBound" : BoundingType.THROUGH_ALL, "oppositeDirection" : true, "depth" : 25 * mm, "offsetDistance" : 25 * mm});
        }
        {
            var Q0;
            Q0=makeQuery(id+"F3.opExtrude","SWEPT_FACE",FACE,{"disambiguationData":[OSD([sQuery(id+"F2.wireOp",EDGE,"E1.2")])]});
            var sketch = newSketch(context, id + "F19", { "sketchPlane" : qUnion([Q0])});
            skLineSegment(sketch, "E124", {"start": v(-16.4, 9.8) * mm, "end": v(16.4, 9.8) * mm});
            skLineSegment(sketch, "E125.0", {"start": v(16.4, 9.8) * mm, "end": v(16.28, 8.14) * mm});
            skLineSegment(sketch, "E126.0", {"start": v(-16.28, 8.14) * mm, "end": v(-16.4, 9.8) * mm});
            skLineSegment(sketch, "E127.0", {"start": v(11.3, 3.5) * mm, "end": v(-11.3, 3.5) * mm});
            skPoint(sketch, "E128.orphan", {"position": v(-5.42, 3.5) * mm});
            skPoint(sketch, "E129.orphan", {"position": v(5.42, 3.5) * mm});
            skPoint(sketch, "E130.visualSharp", {"position": v(-15.95, 3.5) * mm});
            skArc(sketch, "E130.filletArc", {"start": v(-16.28, 8.14) * mm, "mid": v(-14.7, 4.84) * mm, "end": v(-11.3, 3.5) * mm});
            skPoint(sketch, "E131.visualSharp", {"position": v(15.95, 3.5) * mm});
            skArc(sketch, "E131.filletArc", {"start": v(11.3, 3.5) * mm, "mid": v(14.7, 4.84) * mm, "end": v(16.28, 8.14) * mm});
            skSolve(sketch);
        }
        {
            var Q0;
            Q0 = qSketchRegion(id + "F19", true);
            extrude(context, id + "F20", {"entities" : qUnion([Q0]), "operationType" : NewBodyOperationType.REMOVE, "endBound" : BoundingType.UP_TO_NEXT, "oppositeDirection" : true, "depth" : 25 * mm, "offsetDistance" : 25 * mm});
        }
        {
            var Q0;
            {var subQ0=sQuery(id+"F2.wireOp",EDGE,"E8");var subQ1=sQuery(id+"F2.wireOp",EDGE,"E7");var subQ2=sQuery(id+"F2.wireOp",EDGE,"E3");var subQ3=sQuery(id+"F2.wireOp",EDGE,"E0.right");Q0=makeQuery(id+"F16.boolean.opBoolean","MERGE",FACE,{"derivedFrom":[makeQuery(id+"F5.boolean.opBoolean","SPLIT",FACE,{"disambiguationData":[TD([makeQuery(id+"F3.opExtrude","SWEPT_FACE",FACE,{"disambiguationData":[OSD([subQ2])]})])],"derivedFrom":makeQuery(id+"F3.opExtrude","CAP_FACE",FACE,{"disambiguationData":[OSD([sQuery(id+"F2.wireOp",EDGE,"E0.bottom"),sQuery(id+"F2.wireOp",EDGE,"E0.top"),sQuery(id+"F2.wireOp",EDGE,"E0.left"),subQ3,sQuery(id+"F2.wireOp",EDGE,"E1.0"),sQuery(id+"F2.wireOp",EDGE,"E1.1"),sQuery(id+"F2.wireOp",EDGE,"E1.2"),sQuery(id+"F2.wireOp",EDGE,"E1.3"),subQ2,sQuery(id+"F2.wireOp",EDGE,"E4"),subQ1,subQ0,sQuery(id+"F2.wireOp",EDGE,"E9"),sQuery(id+"F2.wireOp",EDGE,"E10"),sQuery(id+"F2.wireOp",EDGE,"E11.trimOffspring"),sQuery(id+"F2.wireOp",EDGE,"E12.trimOffspring"),sQuery(id+"F2.wireOp",EDGE,"E13.filletArc"),sQuery(id+"F2.wireOp",EDGE,"E14.filletArc"),sQuery(id+"F2.wireOp",EDGE,"E15.filletArc"),sQuery(id+"F2.wireOp",EDGE,"E16.filletArc"),sQuery(id+"F2.wireOp",EDGE,"E17.filletArc"),sQuery(id+"F2.wireOp",EDGE,"E18.filletArc"),sQuery(id+"F2.wireOp",EDGE,"E19.filletArc"),sQuery(id+"F2.wireOp",EDGE,"E20.filletArc"),sQuery(id+"F2.wireOp",EDGE,"E25"),sQuery(id+"F2.wireOp",EDGE,"E26"),sQuery(id+"F2.wireOp",EDGE,"E29"),sQuery(id+"F2.wireOp",EDGE,"E30"),sQuery(id+"F2.wireOp",EDGE,"E31"),sQuery(id+"F2.wireOp",EDGE,"E32"),sQuery(id+"F2.wireOp",EDGE,"E33.trimOffspring"),sQuery(id+"F2.wireOp",EDGE,"E34.trimOffspring"),sQuery(id+"F2.wireOp",EDGE,"E35.filletArc"),sQuery(id+"F2.wireOp",EDGE,"E36.filletArc"),sQuery(id+"F2.wireOp",EDGE,"E37.filletArc"),sQuery(id+"F2.wireOp",EDGE,"E38.filletArc")])],"isStart":false})}),makeQuery(id+"F16.opExtrude","CAP_FACE",FACE,{"disambiguationData":[OSD([sQuery(id+"F15.wireOp",EDGE,"E111"),sQuery(id+"F15.wireOp",EDGE,"E113.0")])],"isStart":true})]});}
            var sketch = newSketch(context, id + "F21", { "sketchPlane" : qUnion([Q0])});
            skCircle(sketch, "E132", {"center": v(-19.4, 7.3) * mm, "radius": 2.1 * mm});
            skCircle(sketch, "E133.0", {"center": v(19.4, 7.3) * mm, "radius": 0.7 * mm, "construction": true});
            skCircle(sketch, "E134", {"center": v(19.4, 7.3) * mm, "radius": 2.1 * mm});
            skSolve(sketch);
        }
        {
            var Q0;
            Q0 = qSketchRegion(id + "F21", true);
            extrude(context, id + "F22", {"entities" : qUnion([Q0]), "operationType" : NewBodyOperationType.REMOVE, "oppositeDirection" : true, "depth" : 1 * mm, "offsetDistance" : 25 * mm});
        }
    });
